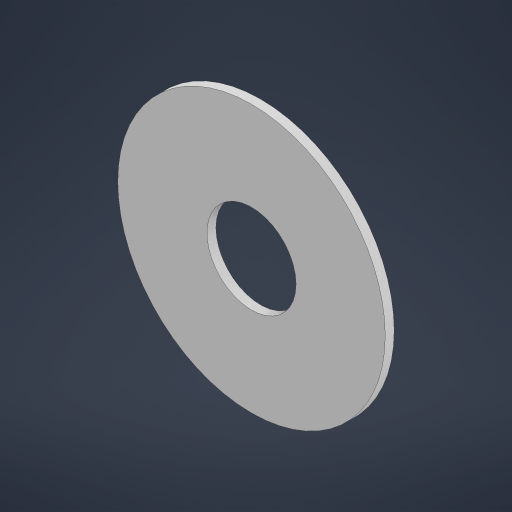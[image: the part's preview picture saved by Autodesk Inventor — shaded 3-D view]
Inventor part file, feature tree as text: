
AUTODESK INVENTOR PART (.ipt)
format: ipt  version: 2023 (Build 270158000, 158)  size: 165,888 bytes
history: native  units: mm
features: sketch x2, extrude x1, hole x1
ambient origin geometry x8: Origin, YZ Plane, XZ Plane, XY Plane, X Axis, Y Axis, Z Axis, Center Point
bodies: Solid1 (feature_tree)
feature tree (4):
  extrude  "Extrusion1"  Depth=1.0mm TaperAngle=0.0deg
  hole  "Hole1"  [1 undecoded]
  sketch  "Sketch1"  dims[d0=30.0mm d1=1.0mm d2=0.0mm]
  sketch  "Sketch2"  dims[d3=10.0mm d4=6.0mm d5=4.0mm d6=2.0mm d7=90.0deg d8=4.0mm d9=0.0mm]
note: 1 required parameter value undecoded (feature->parameter linkage not recoverable at this tier; creation-order binding heuristic only, values carry confidence <= 0.55)
